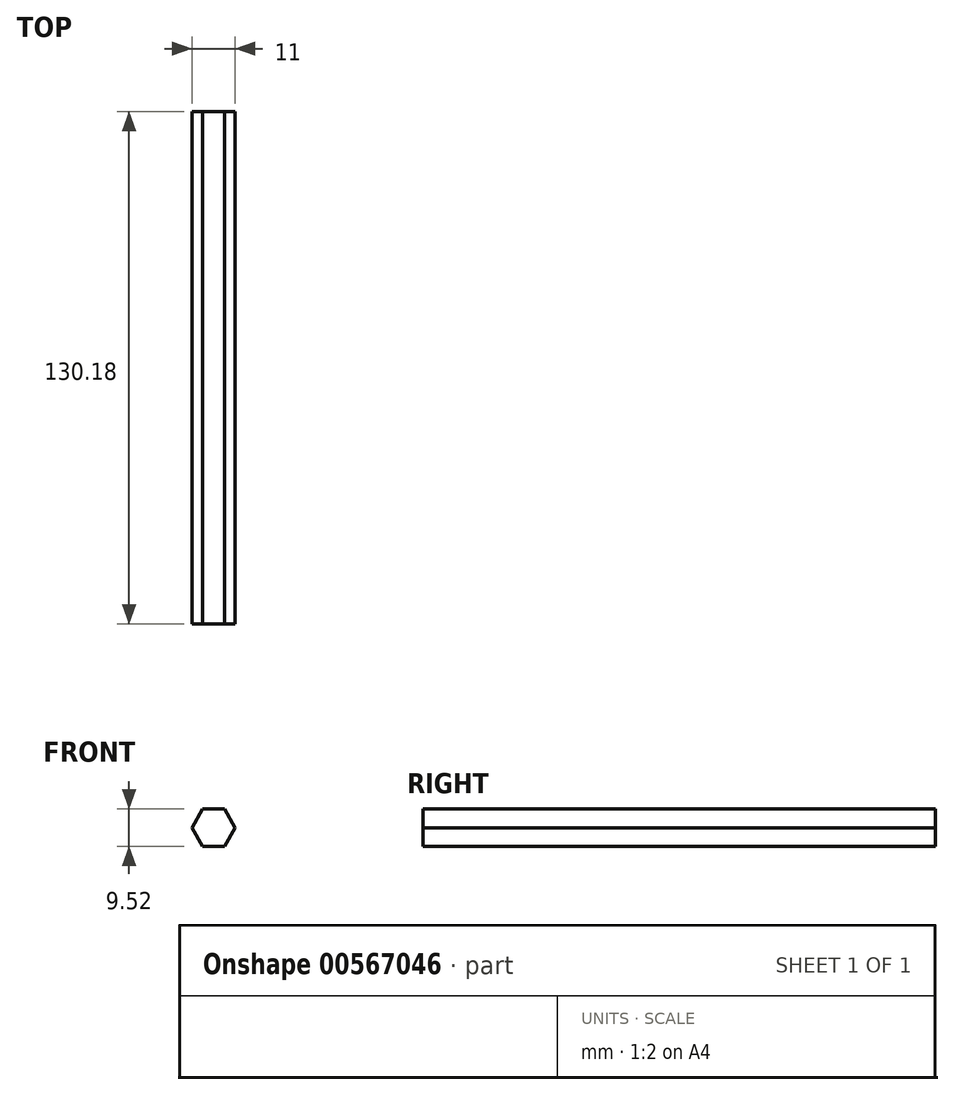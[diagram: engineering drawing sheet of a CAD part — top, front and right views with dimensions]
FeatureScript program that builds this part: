
annotation { "Feature Type Name" : "Feature", "Feature Type Description" : "" }
export const myFeature = defineFeature(function(context is Context, id is Id, definition is map)
    precondition{}
    {
        {
            var Q0;
            Q0=qCreatedBy(makeId("Front.planeOp"),FACE);
            var sketch = newSketch(context, id + "F0", { "sketchPlane" : qUnion([Q0])});
            skCircle(sketch, "E0.cCircle", {"center": v(0, 0) * mm, "radius": 4.76 * mm, "construction": true});
            skLineSegment(sketch, "E0.0", {"start": v(-2.75, 4.76) * mm, "end": v(2.75, 4.76) * mm});
            skLineSegment(sketch, "E0.1", {"start": v(2.75, 4.76) * mm, "end": v(5.5, 0) * mm});
            skLineSegment(sketch, "E0.2", {"start": v(5.5, 0) * mm, "end": v(2.75, -4.76) * mm});
            skLineSegment(sketch, "E0.3", {"start": v(2.75, -4.76) * mm, "end": v(-2.75, -4.76) * mm});
            skLineSegment(sketch, "E0.4", {"start": v(-2.75, -4.76) * mm, "end": v(-5.5, 0) * mm});
            skLineSegment(sketch, "E0.5", {"start": v(-5.5, 0) * mm, "end": v(-2.75, 4.76) * mm});
            skPoint(sketch, "E0.0.midPoint", {"position": v(0, 4.76) * mm});
            skSolve(sketch);
        }
        {
            var Q0;
            Q0 = qSketchRegion(id + "F0", true);
            extrude(context, id + "F1", {"entities" : qUnion([Q0]), "depth" : 130.17 * mm, "offsetDistance" : 25.4 * mm});
        }
    });
